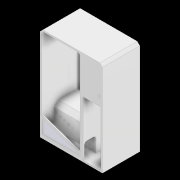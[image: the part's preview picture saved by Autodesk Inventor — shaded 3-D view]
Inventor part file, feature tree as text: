
AUTODESK INVENTOR PART (.ipt)
format: ipt  version: 2020 (Build 240168000, 168)  size: 180,224 bytes
history: native  units: mm
features: plane x6, other x5, chamfer x1
ambient origin geometry x8: Origin, YZ Plane, XZ Plane, XY Plane, X Axis, Y Axis, Z Axis, Center Point
bodies: Body1 (feature_tree)
feature tree (12):
  other  "自動販賣機.ipt"
  plane  "工作平面1"
  plane  "工作平面2"
  plane  "工作平面3"
  plane  "工作平面4"
  plane  "工作平面6"
  chamfer  "倒角1"  Distance=10.0mm
  other  "實體3::自動販賣機.ipt"
  other  "標籤特徵1"
  other  "工作軸線1"
  plane  "工作平面5"
  other  "實體1"
